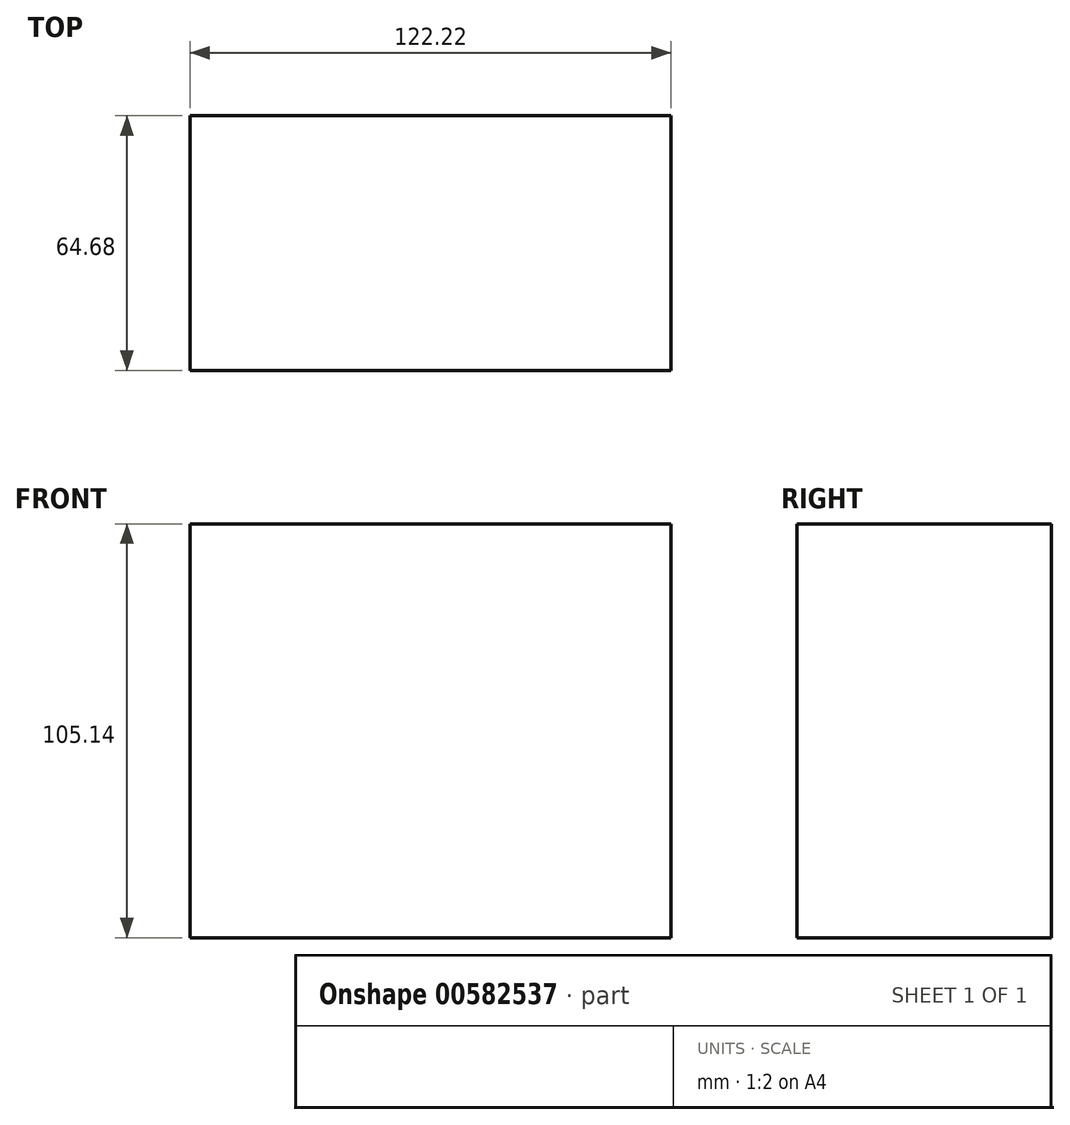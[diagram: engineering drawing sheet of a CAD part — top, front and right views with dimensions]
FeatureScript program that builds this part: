
annotation { "Feature Type Name" : "Feature", "Feature Type Description" : "" }
export const myFeature = defineFeature(function(context is Context, id is Id, definition is map)
    precondition{}
    {
        {
            var Q0;
            Q0=qCreatedBy(makeId("Front.planeOp"),FACE);
            var sketch = newSketch(context, id + "F0", { "sketchPlane" : qUnion([Q0])});
            skLineSegment(sketch, "E0.bottom", {"start": v(61.11, 52.57) * mm, "end": v(-61.11, 52.57) * mm});
            skLineSegment(sketch, "E0.top", {"start": v(61.11, -52.57) * mm, "end": v(-61.11, -52.57) * mm});
            skLineSegment(sketch, "E0.left", {"start": v(61.11, 52.57) * mm, "end": v(61.11, -52.57) * mm});
            skLineSegment(sketch, "E0.right", {"start": v(-61.11, 52.57) * mm, "end": v(-61.11, -52.57) * mm});
            skPoint(sketch, "E0.middle", {"position": v(0, 0) * mm});
            skSolve(sketch);
        }
        {
            var Q0;
            Q0 = qSketchRegion(id + "F0", true);
            extrude(context, id + "F1", {"entities" : qUnion([Q0]), "depth" : 64.68 * mm, "offsetDistance" : 25.4 * mm});
        }
    });
